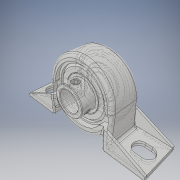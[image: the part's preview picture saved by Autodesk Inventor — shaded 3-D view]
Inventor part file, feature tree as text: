
AUTODESK INVENTOR PART (.ipt)
format: ipt  version: 2019 (Build 230136000, 136)  size: 564,736 bytes
history: native  units: in
note: dims shown in document units (in); Inventor stores cm internally (conversion verified against a paired STEP export)
features: other x4, fillet x1, pattern_circular x1
ambient origin geometry x8: Origin, YZ Plane, XZ Plane, XY Plane, X Axis, Y Axis, Z Axis, Center Point
bodies: Solid1 (feature_tree), Solid2 (feature_tree), Solid3 (feature_tree), Solid4 (feature_tree), Solid5 (feature_tree), Solid6 (feature_tree)
feature tree (6):
  other  "Cut-Revolve1"
  fillet  "Fillet7"  [1 undecoded]
  other  "Cut-Extrude7"
  pattern_circular  "CirPattern2"
  other  "Cut-Extrude1[1]"
  other  "Cut-Extrude1[2]"
note: 1 required parameter value undecoded (feature->parameter linkage not recoverable at this tier; creation-order binding heuristic only, values carry confidence <= 0.55)
